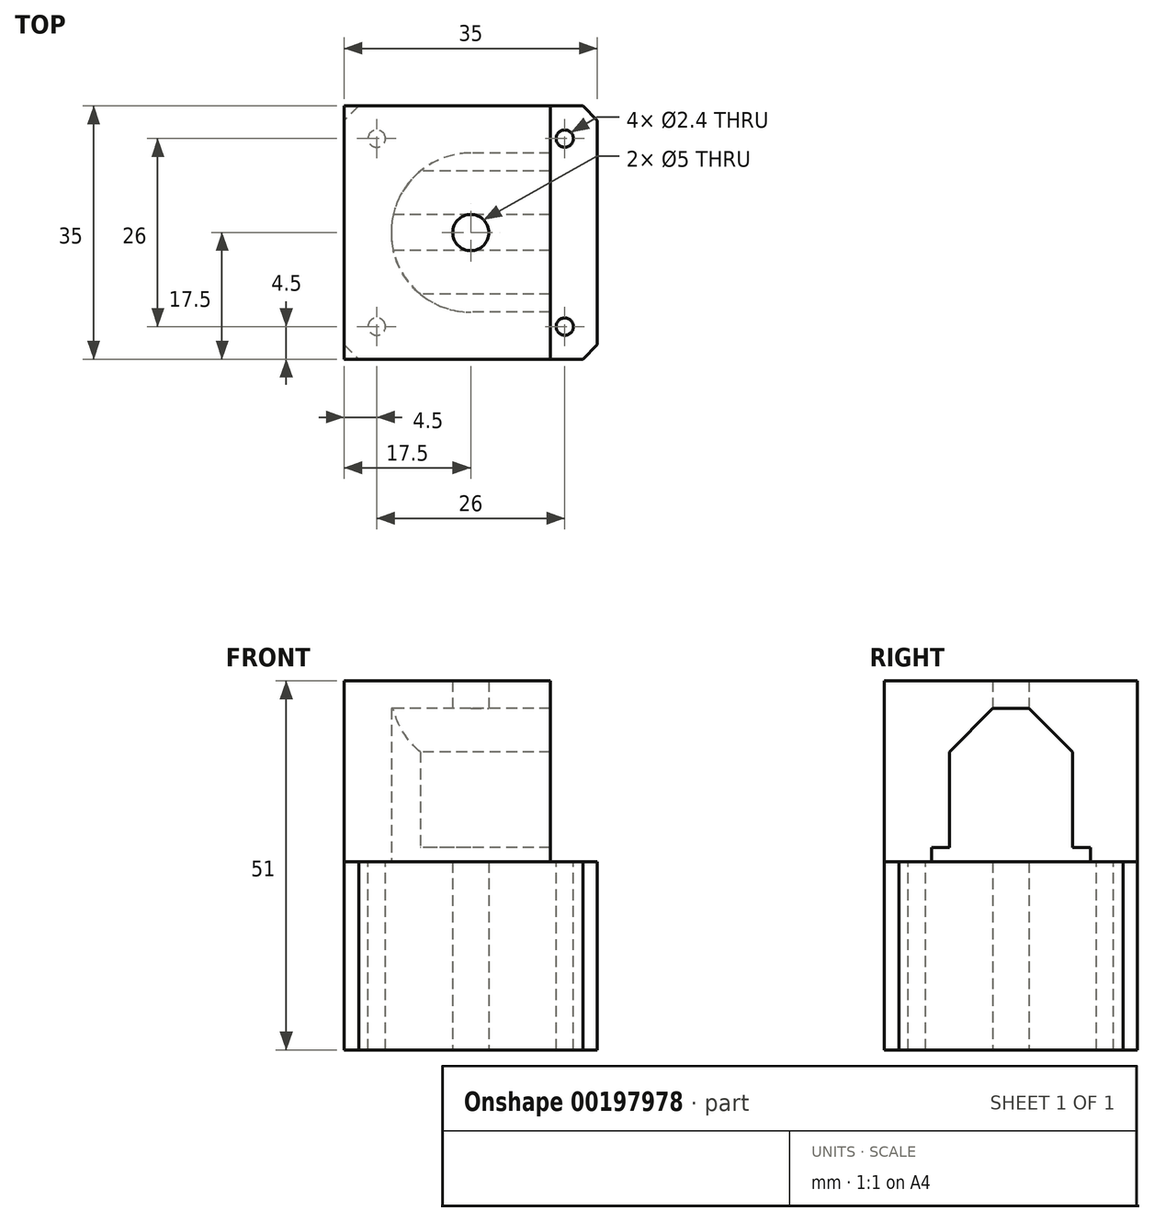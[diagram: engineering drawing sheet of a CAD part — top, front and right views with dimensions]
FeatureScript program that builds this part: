
annotation { "Feature Type Name" : "Feature", "Feature Type Description" : "" }
export const myFeature = defineFeature(function(context is Context, id is Id, definition is map)
    precondition{}
    {
        {
            var Q0;
            Q0=qCreatedBy(makeId("Top.planeOp"),FACE);
            var sketch = newSketch(context, id + "F0", { "sketchPlane" : qUnion([Q0])});
            skCircle(sketch, "E0", {"center": v(0, 0) * mm, "radius": 11 * mm});
            skLineSegment(sketch, "E1.bottom", {"start": v(-17.5, 17.5) * mm, "end": v(17.5, 17.5) * mm});
            skLineSegment(sketch, "E1.top", {"start": v(-17.5, -17.5) * mm, "end": v(17.5, -17.5) * mm});
            skLineSegment(sketch, "E1.left", {"start": v(-17.5, 17.5) * mm, "end": v(-17.5, -17.5) * mm});
            skLineSegment(sketch, "E1.right", {"start": v(17.5, 17.5) * mm, "end": v(17.5, -17.5) * mm});
            skLineSegment(sketch, "E2.bottom", {"start": v(-13, 13) * mm, "end": v(13, 13) * mm, "construction": true});
            skLineSegment(sketch, "E2.top", {"start": v(-13, -13) * mm, "end": v(13, -13) * mm, "construction": true});
            skLineSegment(sketch, "E2.left", {"start": v(-13, 13) * mm, "end": v(-13, -13) * mm, "construction": true});
            skLineSegment(sketch, "E2.right", {"start": v(13, 13) * mm, "end": v(13, -13) * mm, "construction": true});
            skLineSegment(sketch, "E3", {"start": v(-15.5, 17.5) * mm, "end": v(-17.5, 15.5) * mm});
            skLineSegment(sketch, "E4.1.0", {"start": v(-17.5, -15.5) * mm, "end": v(-15.5, -17.5) * mm});
            skLineSegment(sketch, "E4.2.0", {"start": v(15.5, -17.5) * mm, "end": v(17.5, -15.5) * mm});
            skLineSegment(sketch, "E4.3.0", {"start": v(17.5, 15.5) * mm, "end": v(15.5, 17.5) * mm});
            skCircle(sketch, "E5", {"center": v(0, 0) * mm, "radius": 2.5 * mm});
            skSolve(sketch);
        }
        {
            var Q0;
            Q0=makeQuery(id+"F0.imprint","IMPRINT",FACE,{"disambiguationData":[TD([[makeQuery(id+"F0.imprint","IMPRINT",EDGE,{"derivedFrom":sQuery(id+"F0.wireOp",EDGE,"E0")}),1.0]])]});
            extrude(context, id + "F1", {"entities" : qUnion([Q0]), "depth" : 2 * mm});
        }
        {
            var Q0;
            Q0=makeQuery(id+"F0.imprint","IMPRINT",FACE,{"disambiguationData":[TD([[makeQuery(id+"F0.imprint","IMPRINT",EDGE,{"derivedFrom":sQuery(id+"F0.wireOp",EDGE,"E0")}),1.0]])]});
            var Q1;
            Q1=makeQuery(id+"F0.imprint","IMPRINT",FACE,{"disambiguationData":[TD([[makeQuery(id+"F0.imprint","IMPRINT",EDGE,{"derivedFrom":sQuery(id+"F0.wireOp",EDGE,"E0")}),-1.0]])]});
            extrude(context, id + "F2", {"entities" : qUnion([Q0, Q1]), "operationType" : NewBodyOperationType.ADD, "oppositeDirection" : true, "depth" : 26 * mm});
        }
        {
            var Q0;
            Q0=sQuery(id+"F0.wireOp",VERTEX,"E2.left.start");
            var Q1;
            Q1=sQuery(id+"F0.wireOp",VERTEX,"E2.right.start");
            var Q2;
            Q2=sQuery(id+"F0.wireOp",VERTEX,"E2.right.end");
            var Q3;
            Q3=sQuery(id+"F0.wireOp",VERTEX,"E2.left.end");
            var Q4;
            Q4=makeQuery(id+"F1.opExtrude","SWEPT_BODY",BODY,{"disambiguationData":[OSD([sQuery(id+"F0.wireOp",EDGE,"E0")])]});
            hole(context, id + "F3", {"style" : HoleStyle.SIMPLE, "endStyle" : HoleEndStyle.THROUGH, "standardTappedOrClearance" : lookupTablePath({ "standard" : "ISO", "engagement" : "75%", "pitch" : "0.6 mm", "size" : "M3", "type" : "Tapped" }), "standardBlindInLast" : lookupTablePath({ "standard" : "ISO", "engagement" : "75%", "pitch" : "0.6 mm", "size" : "M3", "type" : "Tapped" }), "holeDiameter" : 2.4 * mm, "startFromSketch" : true, "locations" : qUnion([Q0, Q1, Q2, Q3]), "scope" : qUnion([Q4]), "isTappedThrough" : true, "showTappedDepth" : true});
        }
        {
            var Q0;
            Q0=makeQuery(id+"F0.imprint","IMPRINT",FACE,{"disambiguationData":[TD([[makeQuery(id+"F0.imprint","IMPRINT",EDGE,{"derivedFrom":sQuery(id+"F0.wireOp",EDGE,"E5")}),1.0]])]});
            extrude(context, id + "F4", {"entities" : qUnion([Q0]), "operationType" : NewBodyOperationType.ADD, "depth" : 13 * mm});
        }
        {
            var Q0;
            Q0=makeQuery(id+"F4.opExtrude","CAP_FACE",FACE,{"disambiguationData":[OSD([sQuery(id+"F0.wireOp",EDGE,"E5")])],"isStart":false});
            var sketch = newSketch(context, id + "F5", { "sketchPlane" : qUnion([Q0])});
            skCircle(sketch, "E6", {"center": v(0, 0) * mm, "radius": 8 * mm});
            skCircle(sketch, "E7.0", {"center": v(0, 0) * mm, "radius": 2.5 * mm});
            skSolve(sketch);
        }
        {
            var Q0;
            Q0 = qSketchRegion(id + "F5", true);
            extrude(context, id + "F6", {"entities" : qUnion([Q0]), "oppositeDirection" : true, "depth" : 8 * mm});
        }
        {
            var Q0;
            Q0=qCreatedBy(makeId("Top.planeOp"),FACE);
            var sketch = newSketch(context, id + "F7", { "sketchPlane" : qUnion([Q0])});
            skLineSegment(sketch, "E8.bottom", {"start": v(-11, 17.5) * mm, "end": v(11, 17.5) * mm});
            skLineSegment(sketch, "E8.top", {"start": v(-11, -17.5) * mm, "end": v(11, -17.5) * mm});
            skLineSegment(sketch, "E8.left", {"start": v(-11, 17.5) * mm, "end": v(-11, -17.5) * mm, "construction": true});
            skLineSegment(sketch, "E8.right", {"start": v(11, 17.5) * mm, "end": v(11, -17.5) * mm});
            skPoint(sketch, "E8.middle", {"position": v(0, 0) * mm});
            skPoint(sketch, "E9.0", {"position": v(0, 17.5) * mm});
            skCircle(sketch, "E10.1", {"center": v(0, 0) * mm, "radius": 2.5 * mm});
            skPoint(sketch, "E11.0", {"position": v(-17.5, -17.5) * mm});
            skPoint(sketch, "E11.1", {"position": v(-17.5, 17.5) * mm});
            skLineSegment(sketch, "E12", {"start": v(-11, -17.5) * mm, "end": v(-17.5, -17.5) * mm});
            skLineSegment(sketch, "E13", {"start": v(-17.5, -17.5) * mm, "end": v(-17.5, 17.5) * mm});
            skLineSegment(sketch, "E14", {"start": v(-17.5, 17.5) * mm, "end": v(-11, 17.5) * mm});
            skCircle(sketch, "E15.0", {"center": v(0, 0) * mm, "radius": 11 * mm, "construction": true});
            skSolve(sketch);
        }
        {
            var Q0;
            Q0 = qSketchRegion(id + "F7", true);
            extrude(context, id + "F8", {"entities" : qUnion([Q0]), "depth" : 25 * mm});
        }
        {
            var Q0;
            Q0=qCreatedBy(makeId("Right.planeOp"),FACE);
            var sketch = newSketch(context, id + "F9", { "sketchPlane" : qUnion([Q0])});
            skLineSegment(sketch, "E16", {"start": v(2.5, 21.2) * mm, "end": v(8.5, 15.2) * mm});
            skLineSegment(sketch, "E17", {"start": v(8.5, 15.2) * mm, "end": v(8.5, 2) * mm});
            skLineSegment(sketch, "E18", {"start": v(2.5, 21.2) * mm, "end": v(0, 21.2) * mm});
            skLineSegment(sketch, "E19.MirrorCS", {"start": v(-2.5, 21.2) * mm, "end": v(0, 21.2) * mm});
            skLineSegment(sketch, "E20.MirrorCS", {"start": v(-2.5, 21.2) * mm, "end": v(-8.5, 15.2) * mm});
            skLineSegment(sketch, "E21.MirrorCS", {"start": v(-8.5, 15.2) * mm, "end": v(-8.5, 2) * mm});
            skLineSegment(sketch, "E22.0", {"start": v(-11, 2) * mm, "end": v(11, 2) * mm, "construction": true});
            skLineSegment(sketch, "E23", {"start": v(8.5, 2) * mm, "end": v(11, 2) * mm});
            skLineSegment(sketch, "E24", {"start": v(11, 2) * mm, "end": v(11, 0) * mm});
            skLineSegment(sketch, "E25.MirrorCS", {"start": v(11, 2) * mm, "end": v(-11, 2) * mm, "construction": true});
            skLineSegment(sketch, "E26.MirrorCS", {"start": v(-8.5, 2) * mm, "end": v(-11, 2) * mm});
            skLineSegment(sketch, "E27.MirrorCS", {"start": v(-11, 2) * mm, "end": v(-11, 0) * mm});
            skLineSegment(sketch, "E28", {"start": v(11, 0) * mm, "end": v(-11, 0) * mm});
            skLineSegment(sketch, "E29.0", {"start": v(-2.5, 13) * mm, "end": v(2.5, 13) * mm});
            skSolve(sketch);
        }
        {
            var Q0;
            Q0=makeQuery(id+"F9.imprint","IMPRINT",FACE,{"disambiguationData":[TD([[makeQuery(id+"F9.imprint","IMPRINT",EDGE,{"derivedFrom":sQuery(id+"F9.wireOp",EDGE,"E16")}),-1.0]])]});
            var Q1;
            Q1=makeQuery(id+"F1.opExtrude","SWEPT_FACE",FACE,{"disambiguationData":[OSD([sQuery(id+"F0.wireOp",EDGE,"E0")])]});
            extrude(context, id + "F10", {"entities" : qUnion([Q0]), "operationType" : NewBodyOperationType.REMOVE, "depth" : 25 * mm, "hasSecondDirection" : true, "secondDirectionBound" : SecondDirectionBoundingType.UP_TO_SURFACE, "secondDirectionOppositeDirection" : true, "secondDirectionBoundEntityFace" : qUnion([Q1]), "secondDirectionDepth" : 25 * mm});
        }
    });
